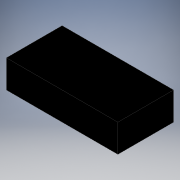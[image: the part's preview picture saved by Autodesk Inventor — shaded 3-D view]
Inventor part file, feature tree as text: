
AUTODESK INVENTOR PART (.ipt)
format: ipt  version: 2016 (Build 200138000, 138)  size: 91,136 bytes
history: native  units: in
note: dims shown in document units (in); Inventor stores cm internally (conversion verified against a paired STEP export)
features: extrude x1, sketch x1
ambient origin geometry x8: Origin, YZ Plane, XZ Plane, XY Plane, X Axis, Y Axis, Z Axis, Center Point
bodies: Solid1 (feature_tree)
feature tree (2):
  extrude  "Extrusion1"  Depth=1.0in
  sketch  "Sketch1"  dims[d0=4.0in d1=1.0in d2=2.0in d3=0.0in]
